# Revit family: FGL
name_source: partatom
category: Lighting Fixtures
units: mm (PartAtom-declared; Revit-internal decimal feet)

## family parameters
Cut with Voids When Loaded = No
Host = Face
Light Source = Yes
OmniClass Number = 23.80.70.14
OmniClass Title = Luminaries for External Lighting
Part Type = Normal
Room Calculation Point = No
Round Connector Dimension = Use Diameter
Shared = No

## types (13) — shared parameters
Apparent Load = 0 VA
Color Filter = 16777215
Default Elevation = 48.000"
Description = Two fitter designs to accommodate architectural requirements
Dimming Lamp Color Temperature Shift = <None>
Emit Shape Visible in Rendering = No
Glass = Glass-Frosted
Lamp = LED Lamp
Load Classification = Lighting
Manufacturer = Architectural Area Lighting
Model = FGL
URL = https://www.currentlighting.com
Watt = 185 W
Wattage Comments = 32 - 185W

## per-type parameters (varying)
| type | Emit from Circle Diameter | Finish | Photometric Web File | Tilt Angle |
| FGL - AWT | 24.000" | Aluminum-Artic White | generic | 60.00° |
| FGL - BLK | 24.000" | Aluminum-Black | generic | 60.00° |
| FGL - MTB | 24.000" | Aluminum-Matte Black | generic | 60.00° |
| FGL - DGN | 24.000" | Aluminum-Dark Green | generic | 60.00° |
| FGL - DBZ | 24.000" | Aluminum-Dark Bronze | generic | 60.00° |
| FGL - WRZ | 12.000" | Aluminum-Weathered Bronze | FGL-SGL-CCO-150PSMH-ASY-HSS.IES | -90.00° |
| FGL - BRM | 24.000" | Aluminum-Metalic Bronze | generic | 60.00° |
| FGL - VBL | 24.000" | Aluminum-Verde Blue | generic | 60.00° |
| FGL - CRT | 24.000" | Aluminum-Corten | generic | 60.00° |
| FGL - MAL | 24.000" | Aluminum-Matte | generic | 60.00° |
| FGL - MDG | 24.000" | Aluminum-Medium Grey | generic | 60.00° |
| FGL - ATG | 24.000" | Aluminum-Antique Green | generic | 60.00° |
| FGL - LGY | 24.000" | Aluminum-Light Grey | generic | 60.00° |

## geometry (parser evidence)
native form markers: Blend x35, Sweep x7
no freeform markers — native parametric forms only
